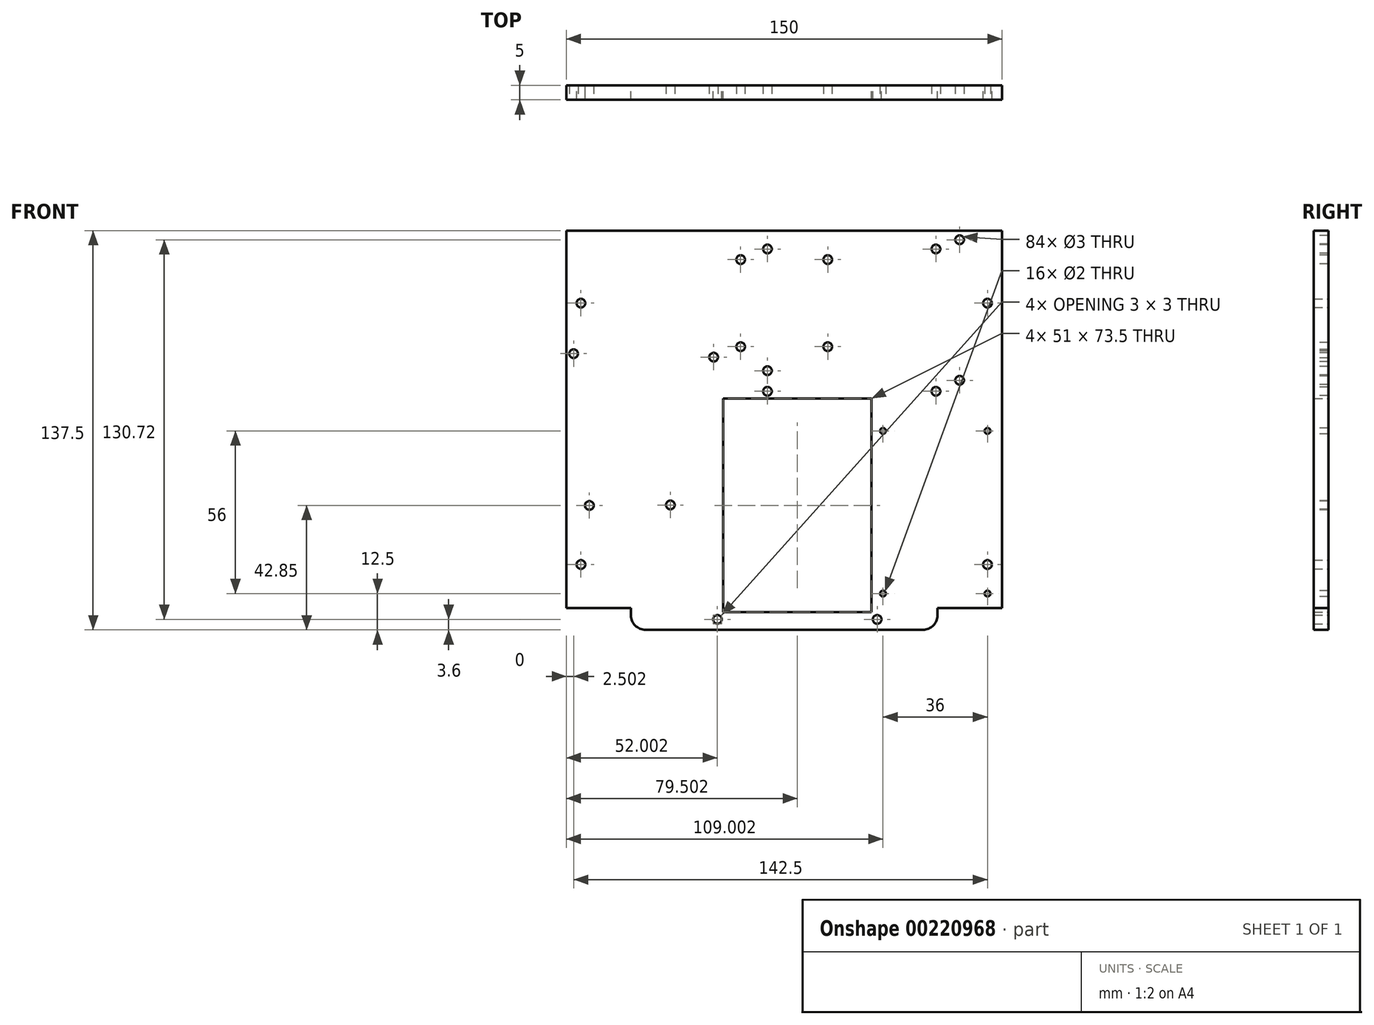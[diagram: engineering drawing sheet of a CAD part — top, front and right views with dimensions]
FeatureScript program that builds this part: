
annotation { "Feature Type Name" : "Feature", "Feature Type Description" : "" }
export const myFeature = defineFeature(function(context is Context, id is Id, definition is map)
    precondition{}
    {
        {
            var Q0;
            Q0=qCreatedBy(makeId("Front.planeOp"),FACE);
            var sketch = newSketch(context, id + "F0", { "sketchPlane" : qUnion([Q0])});
            skLineSegment(sketch, "E0.bottom", {"start": v(3.2, 0) * mm, "end": v(153.2, 0) * mm});
            skLineSegment(sketch, "E0.top", {"start": v(3.2, 130) * mm, "end": v(153.2, 130) * mm});
            skLineSegment(sketch, "E0.left", {"start": v(3.2, 0) * mm, "end": v(3.2, 130) * mm});
            skLineSegment(sketch, "E0.right", {"start": v(153.2, 0) * mm, "end": v(153.2, 130) * mm});
            skLineSegment(sketch, "E1", {"start": v(3.2, 0) * mm, "end": v(3.2, 15) * mm});
            skLineSegment(sketch, "E2", {"start": v(3.2, 15) * mm, "end": v(8.2, 15) * mm});
            skLineSegment(sketch, "E3", {"start": v(8.2, 15) * mm, "end": v(8.2, 105) * mm});
            skCircle(sketch, "E4", {"center": v(8.2, 105) * mm, "radius": 1.5 * mm});
            skCircle(sketch, "E5", {"center": v(8.2, 15) * mm, "radius": 1.5 * mm});
            skLineSegment(sketch, "E6", {"start": v(153.2, 0) * mm, "end": v(153.2, 15) * mm});
            skLineSegment(sketch, "E7", {"start": v(153.2, 15) * mm, "end": v(148.2, 15) * mm});
            skLineSegment(sketch, "E8", {"start": v(148.2, 15) * mm, "end": v(148.2, 105) * mm});
            skCircle(sketch, "E9", {"center": v(148.2, 105) * mm, "radius": 1.5 * mm});
            skCircle(sketch, "E10", {"center": v(148.2, 15) * mm, "radius": 1.5 * mm});
            skLineSegment(sketch, "E11", {"start": v(3.2, 0) * mm, "end": v(25.44, 0) * mm});
            skLineSegment(sketch, "E12", {"start": v(153.2, 0) * mm, "end": v(130.94, 0) * mm});
            skLineSegment(sketch, "E13", {"start": v(25.44, 0) * mm, "end": v(25.44, -7.5) * mm});
            skLineSegment(sketch, "E14", {"start": v(130.94, 0) * mm, "end": v(130.94, -7.5) * mm});
            skLineSegment(sketch, "E15", {"start": v(25.44, -7.5) * mm, "end": v(130.94, -7.5) * mm});
            skSolve(sketch);
        }
        {
            var Q0;
            Q0 = qSketchRegion(id + "F0", true);
            extrude(context, id + "F1", {"entities" : qUnion([Q0]), "depth" : 5 * mm, "offsetDistance" : 25 * mm});
        }
        {
            var Q0;
            Q0=makeQuery(id+"F1.opExtrude","CAP_FACE",FACE,{"disambiguationData":[OSD([sQuery(id+"F0.wireOp",EDGE,"E0.top"),sQuery(id+"F0.wireOp",EDGE,"E0.left"),sQuery(id+"F0.wireOp",EDGE,"E0.right"),sQuery(id+"F0.wireOp",EDGE,"E1"),sQuery(id+"F0.wireOp",EDGE,"E4"),sQuery(id+"F0.wireOp",EDGE,"E5"),sQuery(id+"F0.wireOp",EDGE,"E6"),sQuery(id+"F0.wireOp",EDGE,"E9"),sQuery(id+"F0.wireOp",EDGE,"E10"),sQuery(id+"F0.wireOp",EDGE,"E11"),sQuery(id+"F0.wireOp",EDGE,"E12"),sQuery(id+"F0.wireOp",EDGE,"E13"),sQuery(id+"F0.wireOp",EDGE,"E14"),sQuery(id+"F0.wireOp",EDGE,"E15")])],"isStart":false});
            var sketch = newSketch(context, id + "F2", { "sketchPlane" : qUnion([Q0])});
            skLineSegment(sketch, "E16", {"start": v(3.2, 0) * mm, "end": v(3.2, 101.6) * mm});
            skLineSegment(sketch, "E17", {"start": v(3.2, 101.6) * mm, "end": v(3.2, 87.6) * mm});
            skLineSegment(sketch, "E18", {"start": v(3.2, 87.6) * mm, "end": v(5.7, 87.6) * mm});
            skCircle(sketch, "E19", {"center": v(5.7, 87.6) * mm, "radius": 1.5 * mm});
            skLineSegment(sketch, "E20", {"start": v(3.2, 101.6) * mm, "end": v(56.5, 101.6) * mm});
            skLineSegment(sketch, "E21", {"start": v(5.7, 87.6) * mm, "end": v(5.7, 86.3) * mm});
            skLineSegment(sketch, "E22", {"start": v(5.7, 86.3) * mm, "end": v(10.8, 86.3) * mm});
            skLineSegment(sketch, "E23", {"start": v(10.8, 86.3) * mm, "end": v(38.7, 86.3) * mm});
            skLineSegment(sketch, "E24", {"start": v(38.7, 86.3) * mm, "end": v(53.9, 86.4) * mm});
            skCircle(sketch, "E25", {"center": v(53.9, 86.4) * mm, "radius": 1.5 * mm});
            skLineSegment(sketch, "E26", {"start": v(53.9, 86.4) * mm, "end": v(54.2, 35.6) * mm});
            skLineSegment(sketch, "E27", {"start": v(54.2, 35.6) * mm, "end": v(39, 35.5) * mm});
            skLineSegment(sketch, "E28", {"start": v(39, 35.5) * mm, "end": v(11.1, 35.33) * mm});
            skCircle(sketch, "E29", {"center": v(39, 35.5) * mm, "radius": 1.5 * mm});
            skCircle(sketch, "E30", {"center": v(11.1, 35.33) * mm, "radius": 1.5 * mm});
            skLineSegment(sketch, "E31", {"start": v(153.2, 0) * mm, "end": v(153.2, 5) * mm});
            skLineSegment(sketch, "E32", {"start": v(153.2, 5) * mm, "end": v(148.2, 5) * mm});
            skLineSegment(sketch, "E33", {"start": v(148.2, 5) * mm, "end": v(112.2, 5) * mm});
            skLineSegment(sketch, "E34", {"start": v(112.2, 5) * mm, "end": v(112.2, 61) * mm});
            skLineSegment(sketch, "E35", {"start": v(112.2, 61) * mm, "end": v(148.2, 61) * mm});
            skCircle(sketch, "E36", {"center": v(148.2, 5) * mm, "radius": 1 * mm});
            skCircle(sketch, "E37", {"center": v(112.2, 5) * mm, "radius": 1 * mm});
            skCircle(sketch, "E38", {"center": v(112.2, 61) * mm, "radius": 1 * mm});
            skCircle(sketch, "E39", {"center": v(148.2, 61) * mm, "radius": 1 * mm});
            skLineSegment(sketch, "E40", {"start": v(153.2, 130) * mm, "end": v(138.58, 130) * mm});
            skLineSegment(sketch, "E41", {"start": v(138.58, 130) * mm, "end": v(138.58, 126.82) * mm});
            skLineSegment(sketch, "E42", {"start": v(138.58, 126.82) * mm, "end": v(138.58, 78.43) * mm});
            skLineSegment(sketch, "E43", {"start": v(72.42, 130) * mm, "end": v(72.42, 123.65) * mm});
            skCircle(sketch, "E44", {"center": v(138.58, 78.43) * mm, "radius": 1.5 * mm});
            skCircle(sketch, "E45", {"center": v(138.58, 126.82) * mm, "radius": 1.5 * mm});
            skCircle(sketch, "E46", {"center": v(72.42, 123.65) * mm, "radius": 1.5 * mm});
            skCircle(sketch, "E47", {"center": v(72.42, 81.74) * mm, "radius": 1.5 * mm});
            skLineSegment(sketch, "E48", {"start": v(153.2, 130) * mm, "end": v(129.7, 130) * mm});
            skLineSegment(sketch, "E49", {"start": v(129.7, 130) * mm, "end": v(129.7, 116.5) * mm});
            skLineSegment(sketch, "E50", {"start": v(78.2, 130) * mm, "end": v(78.2, 105) * mm});
            skLineSegment(sketch, "E51", {"start": v(78.2, 105) * mm, "end": v(63.2, 105) * mm});
            skLineSegment(sketch, "E52", {"start": v(63.2, 105) * mm, "end": v(63.2, 120) * mm});
            skCircle(sketch, "E53", {"center": v(63.2, 120) * mm, "radius": 1.5 * mm});
            skCircle(sketch, "E54.1.0", {"center": v(63.2, 90) * mm, "radius": 1.5 * mm});
            skCircle(sketch, "E54.2.0", {"center": v(93.2, 90) * mm, "radius": 1.5 * mm});
            skCircle(sketch, "E54.3.0", {"center": v(93.2, 120) * mm, "radius": 1.5 * mm});
            skPoint(sketch, "E54.center", {"position": v(78.2, 105) * mm});
            skLineSegment(sketch, "E55", {"start": v(93.2, 120) * mm, "end": v(93.2, 130) * mm});
            skLineSegment(sketch, "E56", {"start": v(93.2, 90) * mm, "end": v(93.2, 120) * mm});
            skLineSegment(sketch, "E57", {"start": v(63.2, 90) * mm, "end": v(63.2, 105) * mm});
            skLineSegment(sketch, "E58", {"start": v(72.42, 81.74) * mm, "end": v(72.42, 105) * mm});
            skLineSegment(sketch, "E59", {"start": v(72.42, 123.65) * mm, "end": v(72.42, 74.65) * mm});
            skCircle(sketch, "E60", {"center": v(72.42, 74.65) * mm, "radius": 1.5 * mm});
            skLineSegment(sketch, "E61", {"start": v(72.42, 74.65) * mm, "end": v(130.42, 74.65) * mm});
            skCircle(sketch, "E62", {"center": v(130.42, 74.65) * mm, "radius": 1.5 * mm});
            skLineSegment(sketch, "E63", {"start": v(130.42, 74.65) * mm, "end": v(130.42, 123.65) * mm});
            skCircle(sketch, "E64", {"center": v(130.42, 123.65) * mm, "radius": 1.5 * mm});
            skSolve(sketch);
        }
        {
            var Q0;
            Q0 = qSketchRegion(id + "F2", true);
            extrude(context, id + "F3", {"entities" : qUnion([Q0]), "operationType" : NewBodyOperationType.REMOVE, "oppositeDirection" : true, "depth" : 25 * mm, "offsetDistance" : 25 * mm});
        }
        {
            var Q0;
            Q0=makeQuery(id+"F1.opExtrude","CAP_FACE",FACE,{"disambiguationData":[OSD([sQuery(id+"F0.wireOp",EDGE,"E0.top"),sQuery(id+"F0.wireOp",EDGE,"E0.left"),sQuery(id+"F0.wireOp",EDGE,"E0.right"),sQuery(id+"F0.wireOp",EDGE,"E1"),sQuery(id+"F0.wireOp",EDGE,"E4"),sQuery(id+"F0.wireOp",EDGE,"E5"),sQuery(id+"F0.wireOp",EDGE,"E6"),sQuery(id+"F0.wireOp",EDGE,"E9"),sQuery(id+"F0.wireOp",EDGE,"E10"),sQuery(id+"F0.wireOp",EDGE,"E11"),sQuery(id+"F0.wireOp",EDGE,"E12"),sQuery(id+"F0.wireOp",EDGE,"E13"),sQuery(id+"F0.wireOp",EDGE,"E14"),sQuery(id+"F0.wireOp",EDGE,"E15")])],"isStart":true});
            var sketch = newSketch(context, id + "F4", { "sketchPlane" : qUnion([Q0])});
            skLineSegment(sketch, "E65", {"start": v(-83.1, -1.4) * mm, "end": v(-83.1, 72.1) * mm});
            skLineSegment(sketch, "E66", {"start": v(-83.1, 72.1) * mm, "end": v(-108.2, 72.1) * mm});
            skLineSegment(sketch, "E67", {"start": v(-83.1, 72.1) * mm, "end": v(-57.2, 72.1) * mm});
            skLineSegment(sketch, "E68", {"start": v(-57.2, 72.1) * mm, "end": v(-57.2, -1.4) * mm});
            skLineSegment(sketch, "E69", {"start": v(-108.2, 72.1) * mm, "end": v(-108.2, -1.4) * mm});
            skLineSegment(sketch, "E70", {"start": v(-83.1, -1.4) * mm, "end": v(-57.2, -1.4) * mm});
            skLineSegment(sketch, "E71", {"start": v(-83.1, -1.4) * mm, "end": v(-108.2, -1.4) * mm});
            skLineSegment(sketch, "E72", {"start": v(-55.2, -1.4) * mm, "end": v(-55.2, -3.9) * mm});
            skCircle(sketch, "E73", {"center": v(-55.2, -3.9) * mm, "radius": 1.5 * mm});
            skLineSegment(sketch, "E74", {"start": v(-110.2, -1.4) * mm, "end": v(-110.2, -3.9) * mm});
            skCircle(sketch, "E75", {"center": v(-110.2, -3.9) * mm, "radius": 1.5 * mm});
            skLineSegment(sketch, "E76", {"start": v(-83.1, -1.4) * mm, "end": v(-83.1, -7.5) * mm});
            skLineSegment(sketch, "E77", {"start": v(-55.2, -1.4) * mm, "end": v(-57.2, -1.4) * mm});
            skLineSegment(sketch, "E78", {"start": v(-110.2, -1.4) * mm, "end": v(-108.2, -1.4) * mm});
            skSolve(sketch);
        }
        {
            var Q0;
            Q0 = qSketchRegion(id + "F4", true);
            extrude(context, id + "F5", {"entities" : qUnion([Q0]), "operationType" : NewBodyOperationType.REMOVE, "oppositeDirection" : true, "depth" : 25 * mm, "offsetDistance" : 25 * mm});
        }
        {
            var Q0;
            Q0=makeQuery(id+"F1.opExtrude","SWEPT_EDGE",EDGE,{"disambiguationData":[OSD([sQuery(id+"F0.wireOp",EDGE,"E14"),sQuery(id+"F0.wireOp",EDGE,"E15")])]});
            var Q1;
            Q1=makeQuery(id+"F1.opExtrude","SWEPT_EDGE",EDGE,{"disambiguationData":[OSD([sQuery(id+"F0.wireOp",EDGE,"E13"),sQuery(id+"F0.wireOp",EDGE,"E15")])]});
            fillet(context, id + "F6", {"entities" : qUnion([Q0, Q1]), "radius" : 5 * mm, "tangentPropagation" : true, "allowEdgeOverflow" : false});
        }
    });
